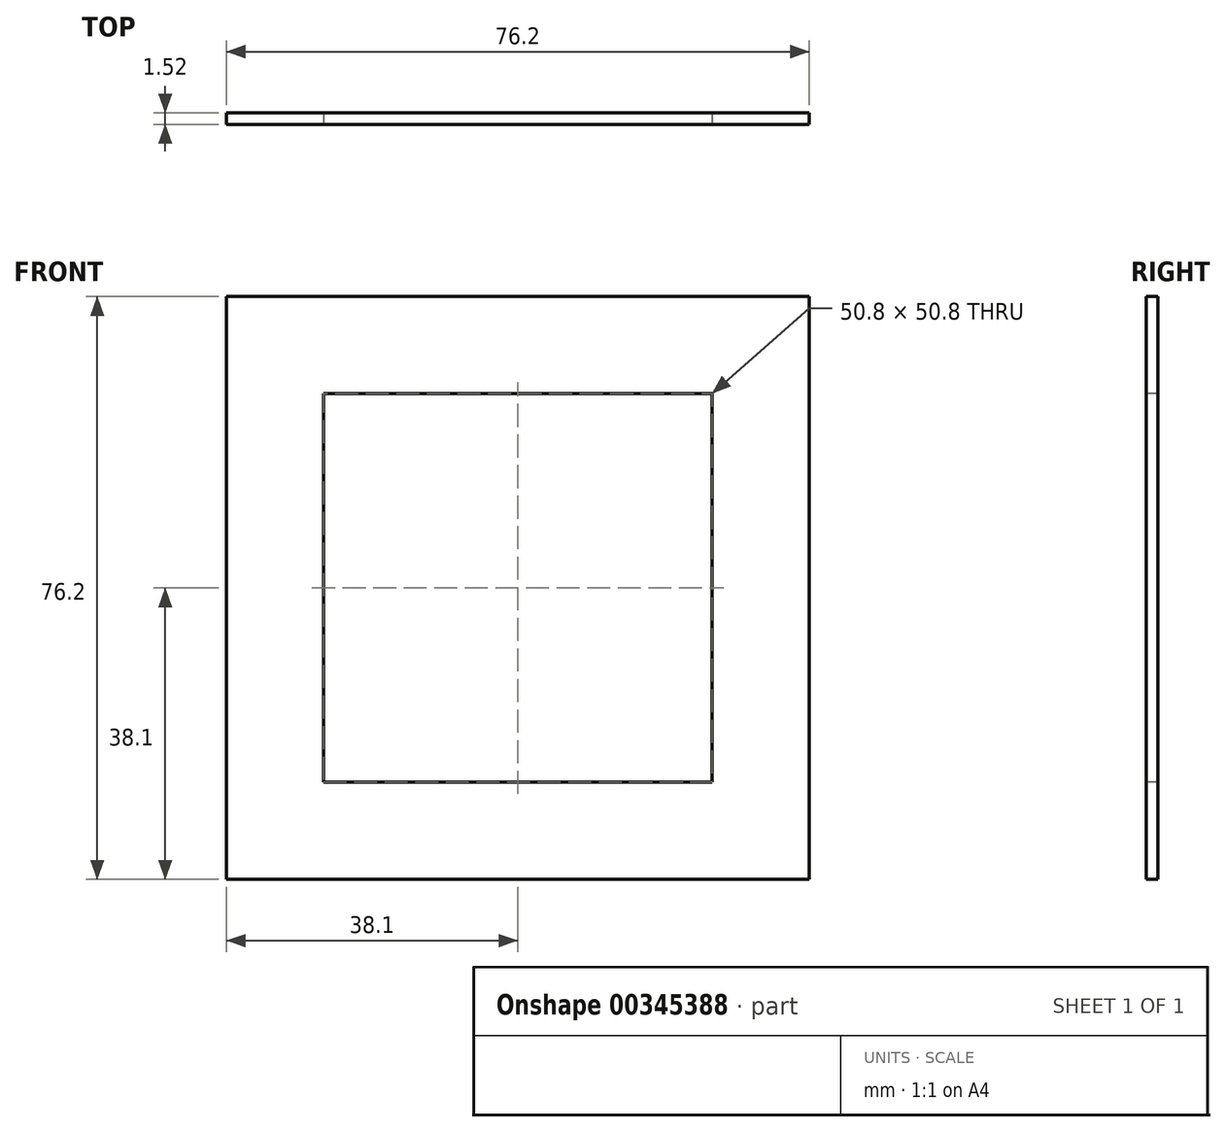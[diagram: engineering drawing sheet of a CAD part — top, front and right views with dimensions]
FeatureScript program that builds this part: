
annotation { "Feature Type Name" : "Feature", "Feature Type Description" : "" }
export const myFeature = defineFeature(function(context is Context, id is Id, definition is map)
    precondition{}
    {
        {
            var Q0;
            Q0=qCreatedBy(makeId("Front.planeOp"),FACE);
            var sketch = newSketch(context, id + "F0", { "sketchPlane" : qUnion([Q0])});
            skLineSegment(sketch, "E0.bottom", {"start": v(-38.1, -38.1) * mm, "end": v(38.1, -38.1) * mm});
            skLineSegment(sketch, "E0.top", {"start": v(-38.1, 38.1) * mm, "end": v(38.1, 38.1) * mm});
            skLineSegment(sketch, "E0.left", {"start": v(-38.1, -38.1) * mm, "end": v(-38.1, 38.1) * mm});
            skLineSegment(sketch, "E0.right", {"start": v(38.1, -38.1) * mm, "end": v(38.1, 38.1) * mm});
            skPoint(sketch, "E0.middle", {"position": v(0, 0) * mm});
            skSolve(sketch);
        }
        {
            var Q0;
            Q0=makeQuery(id+"F0.imprint","IMPRINT",FACE,{"disambiguationData":[TD([[makeQuery(id+"F0.imprint","IMPRINT",EDGE,{"derivedFrom":sQuery(id+"F0.wireOp",EDGE,"E0.bottom")}),1.0]])]});
            extrude(context, id + "F1", {"entities" : qUnion([Q0]), "depth" : 1.52 * mm, "offsetDistance" : 25.4 * mm});
        }
        {
            var Q0;
            Q0=makeQuery(id+"F1.opExtrude","CAP_FACE",FACE,{"disambiguationData":[OSD([sQuery(id+"F0.wireOp",EDGE,"E0.bottom"),sQuery(id+"F0.wireOp",EDGE,"E0.top"),sQuery(id+"F0.wireOp",EDGE,"E0.left"),sQuery(id+"F0.wireOp",EDGE,"E0.right")])],"isStart":false});
            var sketch = newSketch(context, id + "F2", { "sketchPlane" : qUnion([Q0])});
            skSolve(sketch);
        }
        {
            var Q0;
            Q0=makeQuery(id+"F2.imprint","IMPRINT",FACE,{"disambiguationData":[TD([[makeQuery(id+"F2.imprint","IMPRINT",EDGE,{"derivedFrom":makeQuery(id+"F1.opExtrude","CAP_EDGE",EDGE,{"disambiguationData":[OSD([sQuery(id+"F0.wireOp",EDGE,"E0.bottom")])],"isStart":false})}),1.0]])]});
            var sketch = newSketch(context, id + "F3", { "sketchPlane" : qUnion([Q0])});
            skLineSegment(sketch, "E1.bottom", {"start": v(25.4, -25.4) * mm, "end": v(-25.4, -25.4) * mm});
            skLineSegment(sketch, "E1.top", {"start": v(25.4, 25.4) * mm, "end": v(-25.4, 25.4) * mm});
            skLineSegment(sketch, "E1.left", {"start": v(25.4, -25.4) * mm, "end": v(25.4, 25.4) * mm});
            skLineSegment(sketch, "E1.right", {"start": v(-25.4, -25.4) * mm, "end": v(-25.4, 25.4) * mm});
            skPoint(sketch, "E1.middle", {"position": v(0, 0) * mm});
            skSolve(sketch);
        }
        {
            var Q0;
            Q0=makeQuery(id+"F3.imprint","IMPRINT",FACE,{"disambiguationData":[TD([[makeQuery(id+"F3.imprint","IMPRINT",EDGE,{"derivedFrom":sQuery(id+"F3.wireOp",EDGE,"E1.bottom")}),-1.0]])]});
            extrude(context, id + "F4", {"entities" : qUnion([Q0]), "operationType" : NewBodyOperationType.REMOVE, "oppositeDirection" : true, "depth" : 25.4 * mm, "offsetDistance" : 25.4 * mm});
        }
    });
